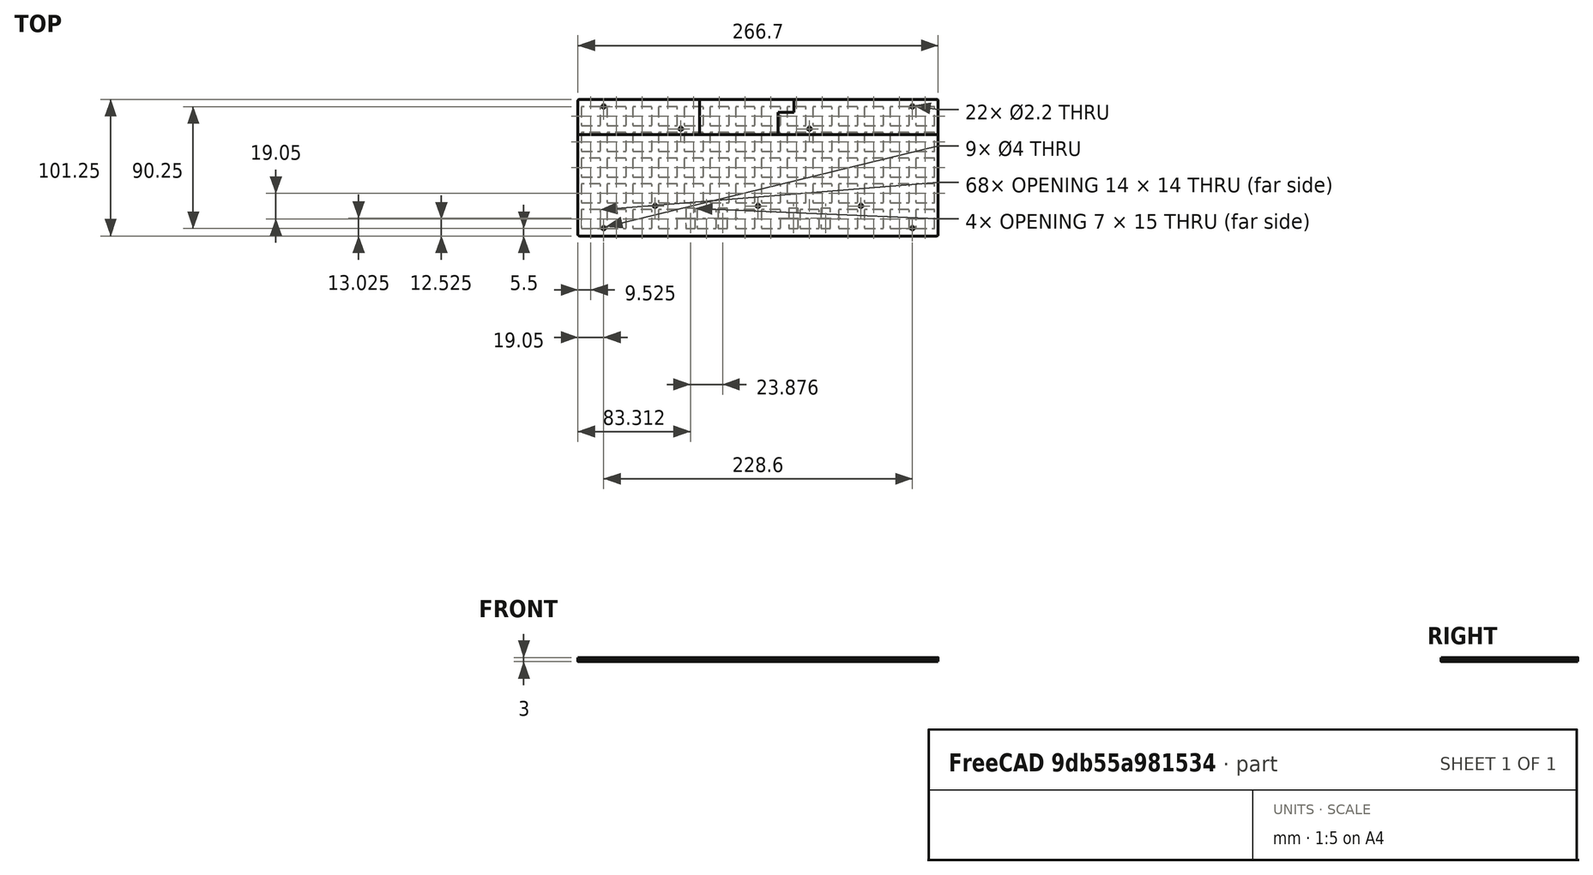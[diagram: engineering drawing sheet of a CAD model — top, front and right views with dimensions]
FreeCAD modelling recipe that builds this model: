
FCSTD DOCUMENT  (FreeCAD 0.20R29177 (Git))
Label: 0-fc-exports
License: All rights reserved
LicenseURL: http://en.wikipedia.org/wiki/All_rights_reserved
objects: App::Part×6, Part::Feature×4, Part::Part2DObjectPython×2
note: 6 computed .brp shape members not serialized (recipe doc carries the construction recipe); baked Part::Feature solids carry a one-line shape summary decoded from their .brp

FEATURE [Part::Feature] Part__Feature  label="plate_part"
  shape: bbox 266.7 x 101.3 x 1.6 mm, 595 faces (baked)
FEATURE [App::Part] plate
  Group = -> [Part__Feature]
  Origin = -> Origin
FEATURE [Part::Feature] Part__Feature001  label="pcb_part"
  shape: bbox 266.7 x 101.3 x 1.6 mm, 19 faces (baked)
FEATURE [App::Part] pcb
  Group = -> [Part__Feature001]
  Origin = -> Origin001
  Placement = pos=(0,0,-5) rot=(0,0,1;0rad)
FEATURE [Part::Feature] Part__Feature002  label="b1_part"
  shape: bbox 266.7 x 101.3 x 3 mm, 25 faces (baked)
FEATURE [App::Part] b1
  Group = -> [Part__Feature002]
  Origin = -> Origin002
  Placement = pos=(-0.0561414,0.0521375,-11) rot=(0,0,1;0rad)
FEATURE [Part::Feature] Part__Feature003  label="b2_part"
  shape: bbox 266.7 x 26 x 3 mm, 14 faces (baked)
FEATURE [App::Part] b2
  Group = -> [Part__Feature003]
  Origin = -> Origin003
  Placement = pos=(0.0561219,-0.0521362,-14) rot=(0,0,1;0rad)
FEATURE [App::Part] cf729e6c_3214_11ed_adba_52540033f8d7  label="cf729e6c-3214-11ed-adba-52540033f8d7"
  Group = -> [plate,pcb,b1,b2]
  Origin = -> Origin004
FEATURE [App::Part] CQ_assembly  label="CQ assembly"
  Group = -> [cf729e6c_3214_11ed_adba_52540033f8d7]
  Origin = -> Origin005
FEATURE [Part::Part2DObjectPython] Shape2DView  # Draft 2D object (typed FeaturePython)
  AutoUpdate = true
  Base = -> b1
  Clip = false
  FuseArch = false
  HiddenLines = false
  InPlace = true
  OnlySolids = false
  Projection = (0,0,1)
  ProjectionMode = 0
  SegmentLength = 0.05
  Tessellation = false
  VisibleOnly = false
FEATURE [Part::Part2DObjectPython] Shape2DView001  # Draft 2D object (typed FeaturePython)
  AutoUpdate = true
  Base = -> b2
  Clip = false
  FuseArch = false
  HiddenLines = false
  InPlace = true
  OnlySolids = false
  Placement = pos=(0,27,0) rot=(0,0,1;0rad)
  Projection = (0,0,1)
  ProjectionMode = 0
  SegmentLength = 0.05
  Tessellation = false
  VisibleOnly = false
